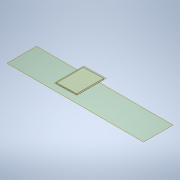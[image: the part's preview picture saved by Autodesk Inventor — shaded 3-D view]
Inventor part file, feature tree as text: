
AUTODESK INVENTOR PART (.ipt)
format: ipt  version: 2020.2 (Build 242310000, 310)  size: 123,904 bytes
history: native  units: mm
features: extrude x3, sketch x3, other x2
ambient origin geometry x8: Origin, YZ Plane, XZ Plane, XY Plane, X Axis, Y Axis, Z Axis, Center Point
bodies: Solide1 (feature_tree)
feature tree (8):
  extrude  "Extrusion1"  Depth=785.7mm
  other  "Plan de construction1"
  extrude  "Extrusion2"  Depth=3.0mm
  other  "Plan de construction2"
  extrude  "Extrusion3"  Depth=65.0mm TaperAngle=0.0deg
  sketch  "Esquisse1"
  sketch  "Esquisse2"
  sketch  "Esquisse3"
